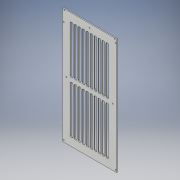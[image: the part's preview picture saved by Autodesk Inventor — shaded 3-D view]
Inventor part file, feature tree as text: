
AUTODESK INVENTOR PART (.ipt)
format: ipt  version: 2017 (Build 210142000, 142)  size: 272,384 bytes
history: native  units: in
note: dims shown in document units (in); Inventor stores cm internally (conversion verified against a paired STEP export)
features: sketch x4, extrude x2, hole x2
ambient origin geometry x8: Origin, YZ Plane, XZ Plane, XY Plane, X Axis, Y Axis, Z Axis, Center Point
bodies: Solid1 (feature_tree)
feature tree (8):
  extrude  "Extrusion1"  Depth=15.0in
  hole  "Hole1"  [1 undecoded]
  extrude  "Extrusion2"  Depth=1.5in
  hole  "Hole2"  [1 undecoded]
  sketch  "Sketch1"  dims[d0=7.016in d1=15.0in]
  sketch  "Sketch2"  dims[d2=0.125in d3=0.0in d4=0.159in]
  sketch  "Sketch3"  dims[d5=0.25in d6=1.5in]
  sketch  "Sketch4"  dims[d7=90.0deg d8=0.125in d9=0.25in d10=0.125in d11=0.25in d12=0.14in d13=0.75in d14=0.375in d15=0.25in d16=0.5635in d17=1.0in d18=0.8108in d19=0.159in d21=0.125in d22=0.5in d23=0.125in d27=1.0in d34=1.0in d39=15.0in d53=7.5in d54=0.25in d55=3.937in d57=0.5157in d58=0.3937in d60=1.0in d62=0.375in d63=5.2094in d64=5.016in d65=1.0in d66=1.0in d67=0.0in d68=15.0in d69=7.5in d70=7.5in d71=1.0in d72=0.5in d73=0.5in d74=7.016in d75=0.5in d76=3.508in d77=0.14in d78=0.75in d79=0.375in d80=0.25in d81=0.5635in d82=1.0in d83=0.8108in]
note: 2 required parameter values undecoded (feature->parameter linkage not recoverable at this tier; creation-order binding heuristic only, values carry confidence <= 0.55)
